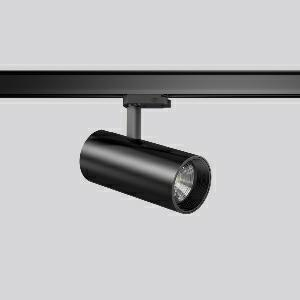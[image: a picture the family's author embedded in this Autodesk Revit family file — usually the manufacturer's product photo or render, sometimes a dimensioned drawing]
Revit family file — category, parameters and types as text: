
# Revit family: deecos_s_mini_742198_003_76_6ecf
name_source: partatom
category: Lighting Fixtures
units: mm (PartAtom-declared; Revit-internal decimal feet)

## family parameters
Cut with Voids When Loaded = No
Host = Face
Light Source = No
Part Type = Normal
Room Calculation Point = No
Round Connector Dimension = Use Diameter
Shared = No

## types (1)
- DEECOS S mini (1 x LED Modul 930, 2250 lm, 3000)
    Apparent Load = 20 VA
    Approval mark = CE
    CIE Flux Codes = 99 100 100 100 100
    Color Rendering = 90
    Color Temperature = 3000
    Default Elevation = 1800 mm
    Description = Series: DEECOS S mini
LED surface-mounted projector in modern design with no visible cooling ribs. Housing: die-cast aluminium, powder-coated. Rotation range: 356°. Swivel range: 90°. Black plastic ring and recessed LED to prevent glare from the side. Optical assembly with lens made of plastic (polycarbonate) for the best homogeneous light distribution - can be changed without tools. Best colour rendering index Ra>90. With adapter for RZB 3-circuit DALI tracks. Suitable for Track on ceiling, Wall track. High quality converter without flickering and stroboscopic effect. The following accessories can be mounted without use of tools: interchangeable lenses, decorative glasses, honeycomb louvre, clear and frosted diffusers, white interchangeable plastic ring. 
Colour: deep black, matt (RAL 9005)
Diameter: 87 mm
Height: 214 mm
Lamp: LED
Socket: without socket
Colour temperature: 3000K
Colour rendering index (CRI): 92
System power: 20 W
Rated luminous flux: 2250 lm
Luminous efficiency: 113 lm/W
Control gear: Converter, dimmable, DALI
Protection class: I
Type of protection: IP 20
    Height = 214 mm
    Lamp = 1 x LED Modul 930
    Lamp Light Flux = 2250 lm
    Lamp count = 1
    Length = 87 mm
    Lifetime = 50000 h
    Luminous efficacy = 113 lm/W
    Manufacturer = RZB
    ModVariant = No
    Model = 742198.003.76
    Mounting Place = Ceiling
    Mounting Type = Rail mounted
    Number of Poles = 1
    OnlyDefault = Yes
    Power Factor = 1
    Product Name = DEECOS S mini
    Product group = Track mounted projectors
    ProductGroupID = 301
    Protection Class = Protection class I
    Protection Degree = IP 20
    RLX_Detail_Level = 1
    RLX_Emergency_Light_Flux = 0 lm
    RLX_Emergency_Type = 0
    RLX_Emergency_Type_DB = No
    RlxData = <blob elided: 38845 chars, md5=697d3477>
    Socket = socket
    Standby Power = 0 W
    System Light Flux = 2250 lm
    System Power = 20 W
    Type Comments = Product without accessories
    Type Image = 741930.003.jpg
    URL = http://relux.com
    VarID = ---
    Voltage = 230 V
    Voltage Range = 220-240 V
    Weight = 0.00 kg
    Width = 0 mm  [stored 0 ft]

note: [stored X ft] marks values corroborated as IEEE doubles in the binary element streams (Revit-internal decimal feet)

## geometry (parser evidence)
native form markers: Blend x4, Sweep x11
no freeform markers — native parametric forms only
